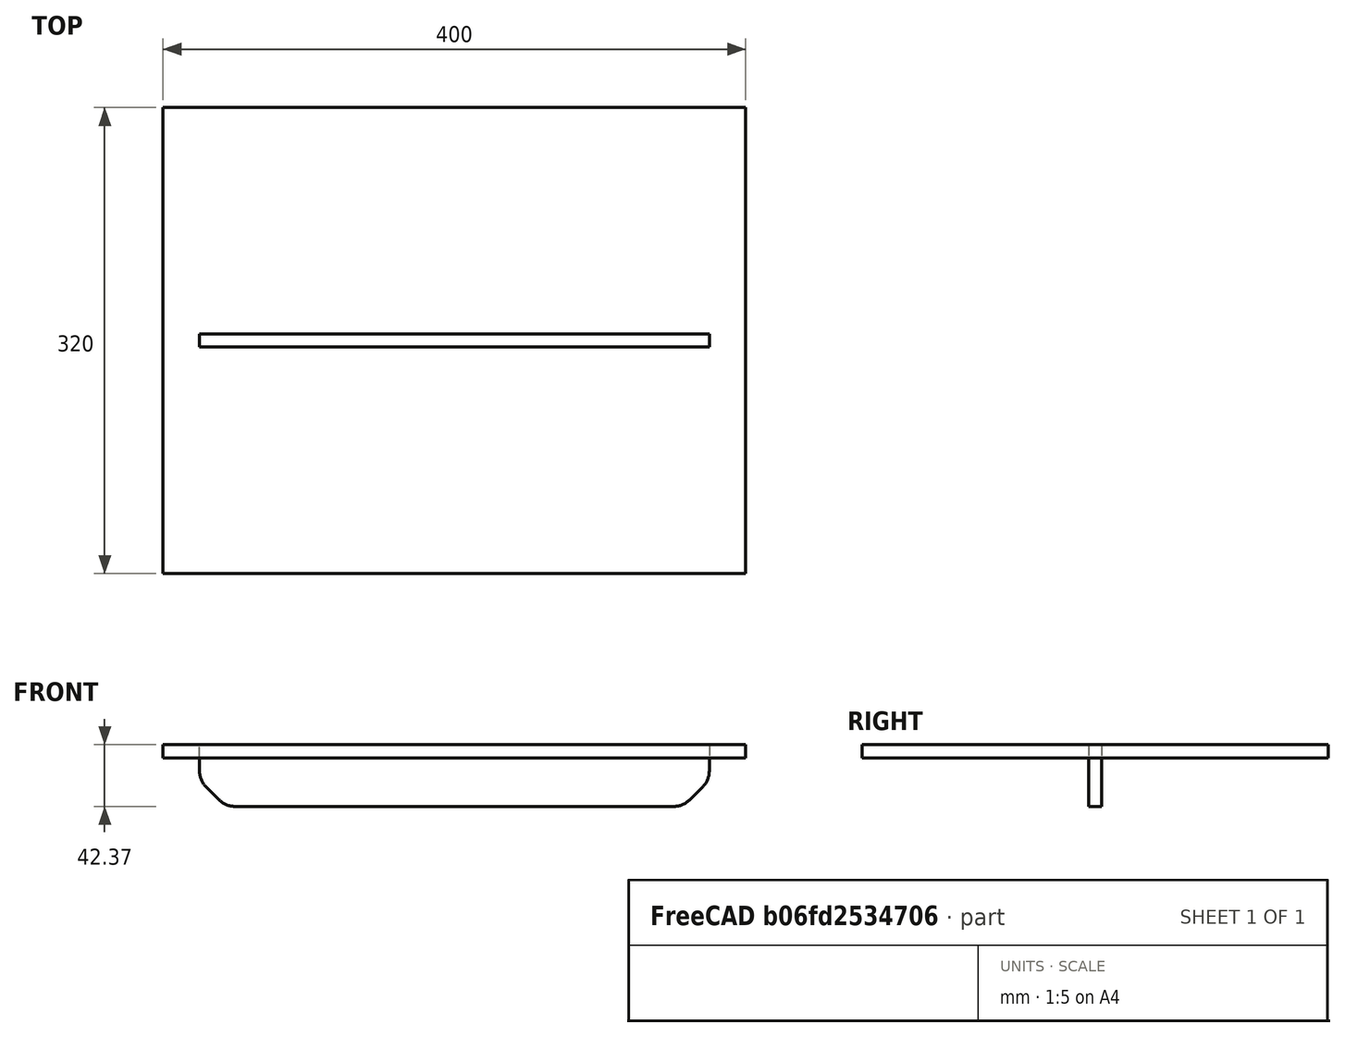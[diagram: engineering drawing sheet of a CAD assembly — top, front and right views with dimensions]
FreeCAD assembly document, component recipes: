
FREECAD ASSEMBLY — COMPONENT RECIPES ("Base_Assembly")

This assembly document has 2 components, labeled P0..P1 below (a component is one placed body or linked part). 2 of them carry a construction recipe — the FreeCAD feature program that regenerates the part from scratch, quoted from this document or its linked companion documents; the rest are supplied as boundary geometry only. No exploded tour is included for this assembly.
COMPONENT P0 — recipe-attached ("Base_bottom", modeled in this document).
Construction recipe (the document's own serialized feature program — sketch geometry with constraints, then the solid features built on it; lengths are millimeters unless a unit is written):

FEATURE [PartDesign::CoordinateSystem] LCS_0001
  AttacherType = Attacher::AttachEngine3D
  MapMode = 2
  Support = -> [X_Axis002]
FEATURE [Sketcher::SketchObject] Sketch001
  FullyConstrained = true
  MapMode = 5
  Support = -> [XY_Plane002]
  expr: Constraints[10] = <<key_dimensions>>#<<Dimensions>>.base_cradle_width
  expr: Constraints[9] = <<key_dimensions>>#<<Dimensions>>.base_cradle_depth
  sketch-geometry (4):
    g0: LineSegment StartX=-200 StartY=160 StartZ=0 EndX=200 EndY=160 EndZ=0
    g1: LineSegment StartX=200 StartY=160 StartZ=0 EndX=200 EndY=-160 EndZ=0
    g2: LineSegment StartX=200 StartY=-160 StartZ=0 EndX=-200 EndY=-160 EndZ=0
    g3: LineSegment StartX=-200 StartY=-160 StartZ=0 EndX=-200 EndY=160 EndZ=0
  constraints (11):
    c: Coincident(g0,g1)
    c: Coincident(g1,g2)
    c: Coincident(g2,g3)
    c: Coincident(g3,g0)
    c: Horizontal(g0)
    c: Horizontal(g2)
    c: Vertical(g1)
    c: Vertical(g3)
    c: Symmetric(g1,g0,g-1)
    c: DistanceY(g3,g3) = 320
    c: DistanceX(g2,g2) = 400
FEATURE [PartDesign::Pad] Pad001
  Direction = (1,1,1)
  Length = 9
  Length2 = 100
  Profile = -> Sketch001
  Reversed = true
  Type = 0
  expr: Length = <<key_dimensions>>#<<Dimensions>>.MDF_thick
FEATURE [PartDesign::Body] Base_bottom
  Group = -> [LCS_0001,Sketch001,Pad001]
  Origin = -> Origin002
  Tip = -> Pad001
COMPONENT P1 — recipe-attached ("Slider_Fixing", modeled in this document).
Construction recipe (the document's own serialized feature program — sketch geometry with constraints, then the solid features built on it; lengths are millimeters unless a unit is written):

FEATURE [PartDesign::CoordinateSystem] LCS_0002
  AttacherType = Attacher::AttachEngine3D
  MapMode = 2
  Support = -> [X_Axis003]
FEATURE [Sketcher::SketchObject] Sketch002
  FullyConstrained = false
  MapMode = 5
  Placement = pos=(0,0,0) rot=(1,0,0;1.5708rad)
  Support = -> [XZ_Plane003]
  sketch-geometry (10):
    g0: LineSegment StartX=-175 StartY=0 StartZ=0 EndX=175 EndY=0 EndZ=0
    g1: LineSegment StartX=175 StartY=0 StartZ=0 EndX=175 EndY=-18.1806 EndZ=0
    g2: LineSegment StartX=170.607 StartY=-28.7872 StartZ=0 EndX=161.414 EndY=-37.9795 EndZ=0
    g3: LineSegment StartX=150.808 StartY=-42.3729 StartZ=0 EndX=-150.808 EndY=-42.3729 EndZ=0
    g4: LineSegment StartX=-161.414 StartY=-37.9795 StartZ=0 EndX=-170.607 EndY=-28.7872 EndZ=0
    g5: LineSegment StartX=-175 StartY=-18.1806 StartZ=0 EndX=-175 EndY=0 EndZ=0
    g6: ArcOfCircle CenterX=-160 CenterY=-18.1806 CenterZ=0 NormalX=0 NormalY=0 NormalZ=1 AngleXU=0 Radius=15 StartAngle=3.14159 EndAngle=3.92699
    g7: ArcOfCircle CenterX=-150.808 CenterY=-27.3729 CenterZ=0 NormalX=0 NormalY=0 NormalZ=1 AngleXU=0 Radius=15 StartAngle=3.92699 EndAngle=4.71239
    g8: ArcOfCircle CenterX=150.808 CenterY=-27.3729 CenterZ=0 NormalX=0 NormalY=0 NormalZ=1 AngleXU=0 Radius=15 StartAngle=4.71239 EndAngle=5.49779
    g9: ArcOfCircle CenterX=160 CenterY=-18.1806 CenterZ=0 NormalX=0 NormalY=0 NormalZ=1 AngleXU=0 Radius=15 StartAngle=5.49779 EndAngle=6.28319
  constraints (24):
    c: Horizontal(g0)
    c: Coincident(g0,g1)
    c: Vertical(g1)
    c: Horizontal(g3)
    c: Vertical(g5)
    c: Coincident(g5,g0)
    c: Equal(g2,g4)
    c: Perpendicular(g4,g2)
    c: Angle(g2) = -2.35619
    c: Symmetric(g0,g0,g-1)
    c: DistanceX(g0,g0) = 350
    c: Tangent(g5,g6) = 1.5708
    c: Tangent(g4,g6) = 1.5708
    c: Tangent(g4,g7) = 1.5708
    c: Tangent(g3,g7) = 1.5708
    c: Equal(g6,g7)
    c: Tangent(g3,g8) = 1.5708
    c: Tangent(g2,g8) = 1.5708
    c: Tangent(g2,g9) = 1.5708
    c: Tangent(g1,g9) = 1.5708
    c: Equal(g9,g8)
    c: Radius(g8) = 15
    c: Equal(g7,g8)
    c: Distance(g2) = 13
FEATURE [PartDesign::Pad] Pad002
  Direction = (1,1,1)
  Length = 9
  Length2 = 100
  Midplane = true
  Placement = pos=(0,0,0) rot=(1,0,0;1.5708rad)
  Profile = -> Sketch002
  Type = 0
  expr: Length = <<key_dimensions>>#<<Dimensions>>.MDF_thick
FEATURE [PartDesign::Body] Slider_Fixing
  Group = -> [LCS_0002,Sketch002,Pad002]
  Origin = -> Origin003
  Tip = -> Pad002
PROVENANCE & LICENSES
A FreeCAD (.FCStd) document from a public repository crawl; recipes are the document's own serialized feature recipes (and, for linked parts, companion documents' recipes).
License: cc-by-sa-4.0.
